# Revit family: Storage-Multi_Level_Workstations-Teknion-BSSRW_Recycling_Waste_Cabinet_for_Sec_Desk-R2018
name_source: partatom
category: Furniture
revit_build: Autodesk Revit 2018 (Build: 20190510_1515(x64)
units: mm (PartAtom-declared; Revit-internal decimal feet)

## family parameters
Always vertical = Yes
Cut with Voids When Loaded = No
OmniClass Number = 23.40.20.00
OmniClass Title = General Furniture and Specialties
Room Calculation Point = No
Shared = Yes
Work Plane-Based = No

## types (4) — shared parameters
Assembly Code = E2020200
Manufacturer = Teknion
Manufacturer Fax = 416.661.4586
Part Number = BSSRW
Position Note = Choose one of the following options below based on the position of the storage cabinet relative to the Secondary Desk.
Product Documentation Link = https://www.teknion.com
Product Line = Expansion Casegoods
Product Page URL = https://www.teknion.com
Series = Expansion Casegoods
Sustainability Data = https://www.teknion.com
URL = www.teknion.com
Unit Weight URL = http://www.teknion.com
Warranty = http://www.teknion.com

## per-type parameters (varying)
| type | Description | Model | Secondary Desk Depth | Secondary Desk Height |
| High Secondary Desk Height, 20" Secondary Desk Depth | Recycling/Waste Cabinet for Secondary Desk, High Secondary Desk Height, 20" Secondary Desk Depth, 18" Width | BSSRW__H2018 | 11.835 " | 25.299 " |
| Low Secondary Desk Height, 20" Secondary Desk Depth | Recycling/Waste Cabinet for Secondary Desk, Low Secondary Desk Height, 20" Secondary Desk Depth, 18" Width | BSSRW__L2018 | 11.835 " | 15.748 " |
| High Secondary Desk Height, 24" Secondary Desk Depth | Recycling/Waste Cabinet for Secondary Desk, High Secondary Desk Height, 24" Secondary Desk Depth, 18" Width | BSSRW__H2418 | 15.835 " | 25.299 " |
| Low Secondary Desk Height, 24" Secondary Desk Depth | Recycling/Waste Cabinet for Secondary Desk, Low Secondary Desk Height, 24" Secondary Desk Depth, 18" Width | BSSRW__L2418 | 15.835 " | 15.748 " |

## geometry (parser evidence)
native form markers: Sweep x2
no freeform markers — native parametric forms only
